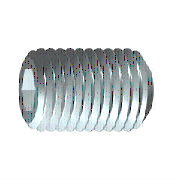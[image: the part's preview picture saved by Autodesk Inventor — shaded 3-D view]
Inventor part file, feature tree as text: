
AUTODESK INVENTOR PART (.ipt)
format: ipt  version: 2018 (Build 220112000, 112)  size: 171,008 bytes
history: native  units: mm (DEFAULTED — no unit token found)
features: sketch x2, extrude x1, other x1, plane x1
ambient origin geometry x8: Origin, YZ Plane, XZ Plane, XY Plane, X Axis, Y Axis, Z Axis, Center Point
bodies: Solid1 (feature_tree), Body (feature_tree)
feature tree (5):
  extrude  "Slot"  TaperAngle=60.0deg  [1 undecoded]
  other  "Work Axis1"
  plane  "Work Plane1"
  sketch  "Sketch1"  dims[d0=2.0mm d1=60.0deg]
  sketch  "Sketch2"  dims[d2=3.0mm d3=1.732051mm d6=90.0deg d4=5.0mm d5=60.0deg d7=2.0mm d8=2.0mm d9=0.0mm d10=0.5mm d11=45.0deg d12=0.306725mm d13=45.0deg d14=5.0mm d15=0.0mm d16=0.0mm d33=0.5mm d34=0.306725mm d35=0.0mm d37=0.0mm]
note: 1 required parameter value undecoded (feature->parameter linkage not recoverable at this tier; creation-order binding heuristic only, values carry confidence <= 0.55)
